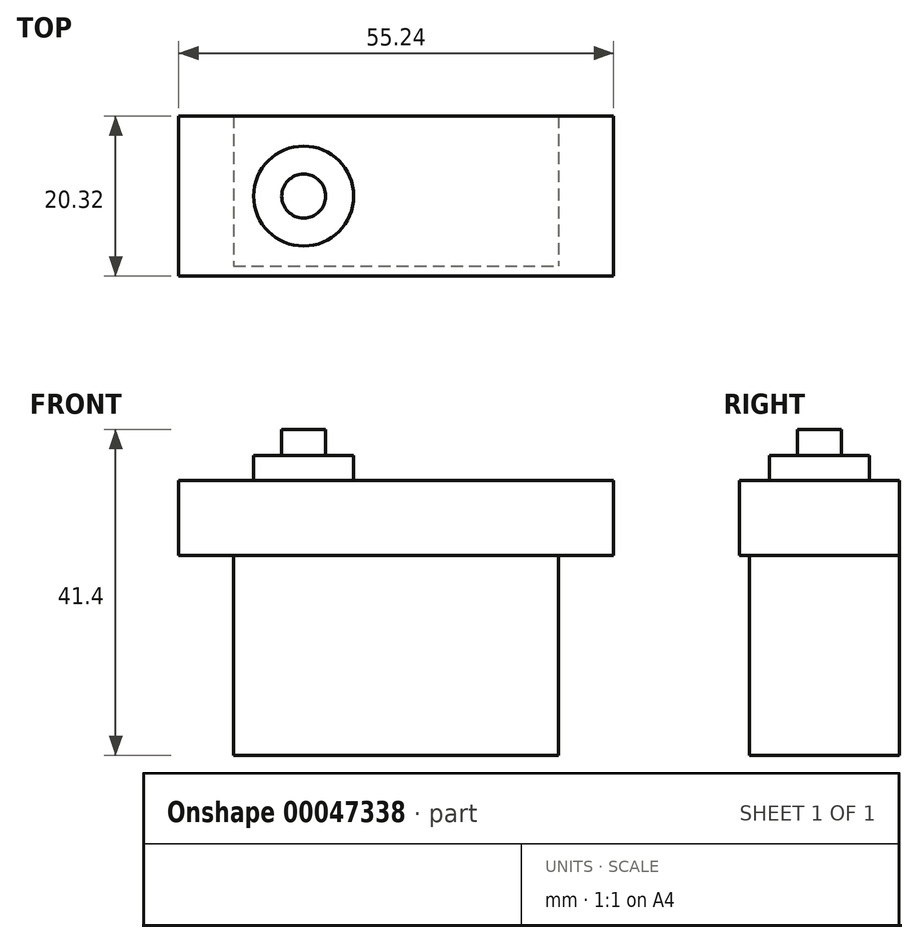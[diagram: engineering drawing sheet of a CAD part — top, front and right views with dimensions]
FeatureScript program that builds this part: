
annotation { "Feature Type Name" : "Feature", "Feature Type Description" : "" }
export const myFeature = defineFeature(function(context is Context, id is Id, definition is map)
    precondition{}
    {
        {
            var Q0;
            Q0=qCreatedBy(makeId("Top.planeOp"),FACE);
            var sketch = newSketch(context, id + "F0", { "sketchPlane" : qUnion([Q0])});
            skLineSegment(sketch, "E0.bottom", {"start": v(-36.88, 17.32) * mm, "end": v(4.4, 17.32) * mm});
            skLineSegment(sketch, "E0.top", {"start": v(-36.88, -1.73) * mm, "end": v(4.4, -1.73) * mm});
            skLineSegment(sketch, "E0.left", {"start": v(-36.88, 17.32) * mm, "end": v(-36.88, -1.73) * mm});
            skLineSegment(sketch, "E0.right", {"start": v(4.4, 17.32) * mm, "end": v(4.4, -1.73) * mm});
            skSolve(sketch);
        }
        {
            var Q0;
            Q0 = qSketchRegion(id + "F0", true);
            extrude(context, id + "F1", {"entities" : qUnion([Q0]), "depth" : 25.4 * mm});
        }
        {
            var Q0;
            Q0=makeQuery(id+"F1.opExtrude","CAP_FACE",FACE,{"disambiguationData":[OSD([sQuery(id+"F0.wireOp",EDGE,"E0.bottom"),sQuery(id+"F0.wireOp",EDGE,"E0.top"),sQuery(id+"F0.wireOp",EDGE,"E0.left"),sQuery(id+"F0.wireOp",EDGE,"E0.right")])],"isStart":false});
            var sketch = newSketch(context, id + "F2", { "sketchPlane" : qUnion([Q0])});
            skLineSegment(sketch, "E1.rect.bottom", {"start": v(11.38, 17.32) * mm, "end": v(-43.86, 17.32) * mm});
            skLineSegment(sketch, "E1.rect.top", {"start": v(11.38, -3) * mm, "end": v(-43.86, -3) * mm});
            skLineSegment(sketch, "E1.rect.left", {"start": v(11.38, 17.32) * mm, "end": v(11.38, -3) * mm});
            skLineSegment(sketch, "E1.rect.right", {"start": v(-43.86, 17.32) * mm, "end": v(-43.86, -3) * mm});
            skLineSegment(sketch, "E2", {"start": v(-36.88, 7.16) * mm, "end": v(-43.86, 7.16) * mm, "construction": true});
            skPoint(sketch, "E2.startSnap0", {"position": v(-43.86, 7.16) * mm});
            skLineSegment(sketch, "E3", {"start": v(4.4, 7.8) * mm, "end": v(11.38, 7.8) * mm, "construction": true});
            skLineSegment(sketch, "E4", {"start": v(-29.53, 17.32) * mm, "end": v(-29.53, 17.32) * mm});
            skSolve(sketch);
        }
        {
            var Q0;
            Q0 = qSketchRegion(id + "F2", true);
            extrude(context, id + "F3", {"entities" : qUnion([Q0]), "operationType" : NewBodyOperationType.ADD, "depth" : 9.52 * mm});
        }
        {
            var Q0;
            Q0=makeQuery(id+"F3.opExtrude","CAP_FACE",FACE,{"disambiguationData":[OSD([sQuery(id+"F2.wireOp",EDGE,"E1.rect.bottom"),sQuery(id+"F2.wireOp",EDGE,"E1.rect.top"),sQuery(id+"F2.wireOp",EDGE,"E1.rect.left"),sQuery(id+"F2.wireOp",EDGE,"E1.rect.right")])],"isStart":false});
            var sketch = newSketch(context, id + "F4", { "sketchPlane" : qUnion([Q0])});
            skLineSegment(sketch, "E5", {"start": v(-27.99, 17.32) * mm, "end": v(-27.99, 7.16) * mm, "construction": true});
            skLineSegment(sketch, "E6", {"start": v(-27.99, 7.16) * mm, "end": v(-27.99, -3) * mm, "construction": true});
            skLineSegment(sketch, "E7", {"start": v(-27.99, 7.16) * mm, "end": v(-43.86, 7.16) * mm, "construction": true});
            skCircle(sketch, "E8", {"center": v(-27.99, 7.16) * mm, "radius": 6.35 * mm});
            skSolve(sketch);
        }
        {
            var Q0;
            Q0 = qSketchRegion(id + "F4", true);
            extrude(context, id + "F5", {"entities" : qUnion([Q0]), "operationType" : NewBodyOperationType.ADD, "depth" : 3.17 * mm});
        }
        {
            var Q0;
            Q0=makeQuery(id+"F5.opExtrude","CAP_FACE",FACE,{"disambiguationData":[OSD([sQuery(id+"F4.wireOp",EDGE,"E8")])],"isStart":false});
            var sketch = newSketch(context, id + "F6", { "sketchPlane" : qUnion([Q0])});
            skLineSegment(sketch, "E9", {"start": v(-27.99, 13.5) * mm, "end": v(-27.99, 7.16) * mm, "construction": true});
            skLineSegment(sketch, "E10", {"start": v(-34.34, 7.16) * mm, "end": v(-27.99, 7.16) * mm, "construction": true});
            skLineSegment(sketch, "E11", {"start": v(-27.99, 7.16) * mm, "end": v(-21.64, 7.16) * mm, "construction": true});
            skLineSegment(sketch, "E12", {"start": v(-27.99, 7.16) * mm, "end": v(-27.99, 0.8) * mm, "construction": true});
            skCircle(sketch, "E13", {"center": v(-27.99, 7.16) * mm, "radius": 2.8 * mm});
            skSolve(sketch);
        }
        {
            var Q0;
            Q0 = qSketchRegion(id + "F6", true);
            extrude(context, id + "F7", {"entities" : qUnion([Q0]), "operationType" : NewBodyOperationType.ADD, "depth" : 3.3 * mm});
        }
    });
